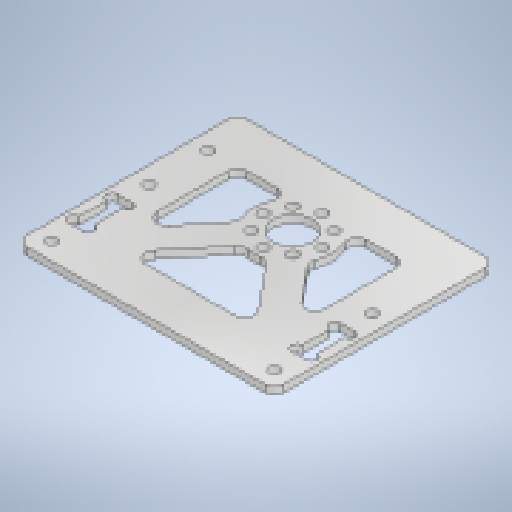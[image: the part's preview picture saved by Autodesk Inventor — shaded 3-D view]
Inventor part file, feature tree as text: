
AUTODESK INVENTOR PART (.ipt)
format: ipt  version: 2025.1 (Build 291241000, 241)  size: 300,544 bytes
history: native  units: mm
features: extrude x3, sketch x3, other x2, fillet x2, projected_geometry x1
ambient origin geometry x8: Origin, YZ Plane, XZ Plane, XY Plane, X Axis, Y Axis, Z Axis, Center Point
bodies: Body1 (feature_tree)
feature tree (11):
  other  "ソリッド1"
  extrude  "押し出し1"  Depth=8.0mm
  extrude  "押し出し2"  Depth=16.0mm
  fillet  "フィレット1"  Radius=12.0mm
  extrude  "押し出し4"  Depth=2.2mm
  fillet  "フィレット3"  Radius=80.0mm
  sketch  "スケッチ1"
  other  "スケッチ円形状パターン1"
  sketch  "スケッチ2"
  sketch  "スケッチ4"
  projected_geometry  "投影ループ2"
